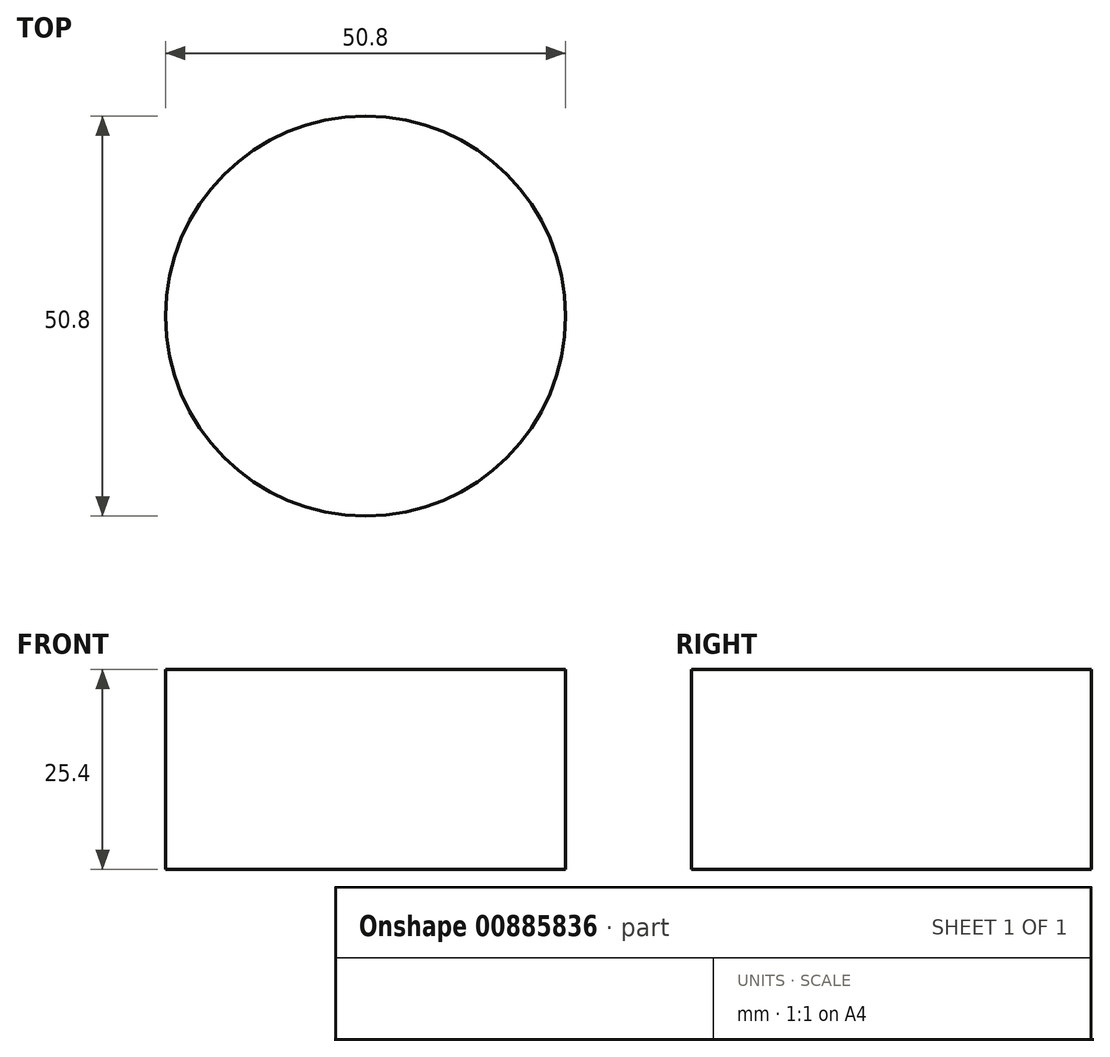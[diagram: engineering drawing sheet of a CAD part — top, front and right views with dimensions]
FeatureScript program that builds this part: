
annotation { "Feature Type Name" : "Feature", "Feature Type Description" : "" }
export const myFeature = defineFeature(function(context is Context, id is Id, definition is map)
    precondition{}
    {
        {
            var Q0;
            Q0=qCreatedBy(makeId("Top.planeOp"),FACE);
            var sketch = newSketch(context, id + "F0", { "sketchPlane" : qUnion([Q0])});
            skCircle(sketch, "E0", {"center": v(0, 0) * mm, "radius": 25.4 * mm});
            skLineSegment(sketch, "E1", {"start": v(76.15, 347.35) * mm, "end": v(71.93, 342.41) * mm});
            skLineSegment(sketch, "E2", {"start": v(71.93, 342.41) * mm, "end": v(67.97, 337.4) * mm});
            skLineSegment(sketch, "E3", {"start": v(67.97, 337.4) * mm, "end": v(64.3, 332.3) * mm});
            skLineSegment(sketch, "E4", {"start": v(64.3, 332.3) * mm, "end": v(60.92, 327.12) * mm});
            skLineSegment(sketch, "E5", {"start": v(60.92, 327.12) * mm, "end": v(57.86, 321.87) * mm});
            skLineSegment(sketch, "E6", {"start": v(57.86, 321.87) * mm, "end": v(55.17, 316.54) * mm});
            skLineSegment(sketch, "E7", {"start": v(55.17, 316.54) * mm, "end": v(52.9, 311.13) * mm});
            skLineSegment(sketch, "E8", {"start": v(52.9, 311.13) * mm, "end": v(51.25, 305.61) * mm});
            skLineSegment(sketch, "E9", {"start": v(51.25, 305.61) * mm, "end": v(49.26, 300.15) * mm});
            skLineSegment(sketch, "E10", {"start": v(49.26, 300.15) * mm, "end": v(35.97, 296.27) * mm});
            skLineSegment(sketch, "E11", {"start": v(35.97, 296.27) * mm, "end": v(24, 303.22) * mm});
            skLineSegment(sketch, "E12", {"start": v(24, 303.22) * mm, "end": v(23.37, 309) * mm});
            skLineSegment(sketch, "E13", {"start": v(23.37, 309) * mm, "end": v(23.09, 314.75) * mm});
            skLineSegment(sketch, "E14", {"start": v(23.09, 314.75) * mm, "end": v(22.19, 320.54) * mm});
            skLineSegment(sketch, "E15", {"start": v(22.19, 320.54) * mm, "end": v(20.84, 326.36) * mm});
            skLineSegment(sketch, "E16", {"start": v(20.84, 326.36) * mm, "end": v(19.13, 332.19) * mm});
            skLineSegment(sketch, "E17", {"start": v(19.13, 332.19) * mm, "end": v(17.1, 338.02) * mm});
            skLineSegment(sketch, "E18", {"start": v(17.1, 338.02) * mm, "end": v(14.74, 343.85) * mm});
            skLineSegment(sketch, "E19", {"start": v(14.74, 343.85) * mm, "end": v(12.1, 349.68) * mm});
            skLineSegment(sketch, "E20", {"start": v(12.1, 349.68) * mm, "end": v(9.2, 355.48) * mm});
            skLineSegment(sketch, "E21", {"start": v(9.2, 355.48) * mm, "end": v(-9.2, 355.48) * mm});
            skLineSegment(sketch, "E22", {"start": v(-9.2, 355.48) * mm, "end": v(-12.1, 349.68) * mm});
            skLineSegment(sketch, "E23", {"start": v(-12.1, 349.68) * mm, "end": v(-14.74, 343.85) * mm});
            skLineSegment(sketch, "E24", {"start": v(-14.74, 343.85) * mm, "end": v(-17.1, 338.02) * mm});
            skLineSegment(sketch, "E25", {"start": v(-17.1, 338.02) * mm, "end": v(-19.13, 332.19) * mm});
            skLineSegment(sketch, "E26", {"start": v(-19.13, 332.19) * mm, "end": v(-20.84, 326.36) * mm});
            skLineSegment(sketch, "E27", {"start": v(-20.84, 326.36) * mm, "end": v(-22.19, 320.54) * mm});
            skLineSegment(sketch, "E28", {"start": v(-22.19, 320.54) * mm, "end": v(-23.09, 314.75) * mm});
            skLineSegment(sketch, "E29", {"start": v(-23.09, 314.75) * mm, "end": v(-23.37, 309) * mm});
            skLineSegment(sketch, "E30", {"start": v(-23.37, 309) * mm, "end": v(-24, 303.22) * mm});
            skLineSegment(sketch, "E31", {"start": v(-24, 303.22) * mm, "end": v(-35.97, 296.27) * mm});
            skLineSegment(sketch, "E32", {"start": v(-35.97, 296.27) * mm, "end": v(-49.26, 300.15) * mm});
            skLineSegment(sketch, "E33", {"start": v(-49.26, 300.15) * mm, "end": v(-51.25, 305.61) * mm});
            skLineSegment(sketch, "E34", {"start": v(-51.25, 305.61) * mm, "end": v(-52.9, 311.13) * mm});
            skLineSegment(sketch, "E35", {"start": v(-52.9, 311.13) * mm, "end": v(-55.17, 316.54) * mm});
            skLineSegment(sketch, "E36", {"start": v(-55.17, 316.54) * mm, "end": v(-57.86, 321.87) * mm});
            skLineSegment(sketch, "E37", {"start": v(-57.86, 321.87) * mm, "end": v(-60.92, 327.12) * mm});
            skLineSegment(sketch, "E38", {"start": v(-60.92, 327.12) * mm, "end": v(-64.3, 332.3) * mm});
            skLineSegment(sketch, "E39", {"start": v(-64.3, 332.3) * mm, "end": v(-67.97, 337.4) * mm});
            skLineSegment(sketch, "E40", {"start": v(-67.97, 337.4) * mm, "end": v(-71.93, 342.41) * mm});
            skLineSegment(sketch, "E41", {"start": v(-71.93, 342.41) * mm, "end": v(-76.15, 347.35) * mm});
            skLineSegment(sketch, "E42", {"start": v(-76.15, 347.35) * mm, "end": v(-94, 342.95) * mm});
            skLineSegment(sketch, "E43", {"start": v(-94, 342.95) * mm, "end": v(-95.44, 336.62) * mm});
            skLineSegment(sketch, "E44", {"start": v(-95.44, 336.62) * mm, "end": v(-96.6, 330.33) * mm});
            skLineSegment(sketch, "E45", {"start": v(-96.6, 330.33) * mm, "end": v(-97.5, 324.11) * mm});
            skLineSegment(sketch, "E46", {"start": v(-97.5, 324.11) * mm, "end": v(-98.08, 317.96) * mm});
            skLineSegment(sketch, "E47", {"start": v(-98.08, 317.96) * mm, "end": v(-98.34, 311.89) * mm});
            skLineSegment(sketch, "E48", {"start": v(-98.34, 311.89) * mm, "end": v(-98.25, 305.92) * mm});
            skLineSegment(sketch, "E49", {"start": v(-98.25, 305.92) * mm, "end": v(-97.74, 300.08) * mm});
            skLineSegment(sketch, "E50", {"start": v(-97.74, 300.08) * mm, "end": v(-96.64, 294.42) * mm});
            skLineSegment(sketch, "E51", {"start": v(-96.64, 294.42) * mm, "end": v(-95.87, 288.66) * mm});
            skLineSegment(sketch, "E52", {"start": v(-95.87, 288.66) * mm, "end": v(-105.83, 279.06) * mm});
            skLineSegment(sketch, "E53", {"start": v(-105.83, 279.06) * mm, "end": v(-119.65, 279.64) * mm});
            skLineSegment(sketch, "E54", {"start": v(-119.65, 279.64) * mm, "end": v(-122.9, 284.47) * mm});
            skLineSegment(sketch, "E55", {"start": v(-122.9, 284.47) * mm, "end": v(-125.83, 289.43) * mm});
            skLineSegment(sketch, "E56", {"start": v(-125.83, 289.43) * mm, "end": v(-129.32, 294.14) * mm});
            skLineSegment(sketch, "E57", {"start": v(-129.32, 294.14) * mm, "end": v(-133.21, 298.66) * mm});
            skLineSegment(sketch, "E58", {"start": v(-133.21, 298.66) * mm, "end": v(-137.43, 303.03) * mm});
            skLineSegment(sketch, "E59", {"start": v(-137.43, 303.03) * mm, "end": v(-141.95, 307.25) * mm});
            skLineSegment(sketch, "E60", {"start": v(-141.95, 307.25) * mm, "end": v(-146.74, 311.32) * mm});
            skLineSegment(sketch, "E61", {"start": v(-146.74, 311.32) * mm, "end": v(-151.78, 315.25) * mm});
            skLineSegment(sketch, "E62", {"start": v(-151.78, 315.25) * mm, "end": v(-157.06, 319.03) * mm});
            skLineSegment(sketch, "E63", {"start": v(-157.06, 319.03) * mm, "end": v(-173.34, 310.5) * mm});
            skLineSegment(sketch, "E64", {"start": v(-173.34, 310.5) * mm, "end": v(-173.22, 304) * mm});
            skLineSegment(sketch, "E65", {"start": v(-173.22, 304) * mm, "end": v(-172.85, 297.62) * mm});
            skLineSegment(sketch, "E66", {"start": v(-172.85, 297.62) * mm, "end": v(-172.22, 291.36) * mm});
            skLineSegment(sketch, "E67", {"start": v(-172.22, 291.36) * mm, "end": v(-171.32, 285.25) * mm});
            skLineSegment(sketch, "E68", {"start": v(-171.32, 285.25) * mm, "end": v(-170.12, 279.3) * mm});
            skLineSegment(sketch, "E69", {"start": v(-170.12, 279.3) * mm, "end": v(-168.6, 273.52) * mm});
            skLineSegment(sketch, "E70", {"start": v(-168.6, 273.52) * mm, "end": v(-166.72, 267.97) * mm});
            skLineSegment(sketch, "E71", {"start": v(-166.72, 267.97) * mm, "end": v(-164.3, 262.74) * mm});
            skLineSegment(sketch, "E72", {"start": v(-164.3, 262.74) * mm, "end": v(-162.17, 257.33) * mm});
            skLineSegment(sketch, "E73", {"start": v(-162.17, 257.33) * mm, "end": v(-169.54, 245.62) * mm});
            skLineSegment(sketch, "E74", {"start": v(-169.54, 245.62) * mm, "end": v(-183.1, 242.88) * mm});
            skLineSegment(sketch, "E75", {"start": v(-183.1, 242.88) * mm, "end": v(-187.4, 246.79) * mm});
            skLineSegment(sketch, "E76", {"start": v(-187.4, 246.79) * mm, "end": v(-191.43, 250.9) * mm});
            skLineSegment(sketch, "E77", {"start": v(-191.43, 250.9) * mm, "end": v(-195.95, 254.64) * mm});
            skLineSegment(sketch, "E78", {"start": v(-195.95, 254.64) * mm, "end": v(-200.81, 258.1) * mm});
            skLineSegment(sketch, "E79", {"start": v(-200.81, 258.1) * mm, "end": v(-205.96, 261.34) * mm});
            skLineSegment(sketch, "E80", {"start": v(-205.96, 261.34) * mm, "end": v(-211.36, 264.35) * mm});
            skLineSegment(sketch, "E81", {"start": v(-211.36, 264.35) * mm, "end": v(-216.98, 267.16) * mm});
            skLineSegment(sketch, "E82", {"start": v(-216.98, 267.16) * mm, "end": v(-222.82, 269.76) * mm});
            skLineSegment(sketch, "E83", {"start": v(-222.82, 269.76) * mm, "end": v(-228.85, 272.18) * mm});
            skLineSegment(sketch, "E84", {"start": v(-228.85, 272.18) * mm, "end": v(-242.6, 259.99) * mm});
            skLineSegment(sketch, "E85", {"start": v(-242.6, 259.99) * mm, "end": v(-240.94, 253.7) * mm});
            skLineSegment(sketch, "E86", {"start": v(-240.94, 253.7) * mm, "end": v(-239.05, 247.6) * mm});
            skLineSegment(sketch, "E87", {"start": v(-239.05, 247.6) * mm, "end": v(-236.94, 241.68) * mm});
            skLineSegment(sketch, "E88", {"start": v(-236.94, 241.68) * mm, "end": v(-234.6, 235.96) * mm});
            skLineSegment(sketch, "E89", {"start": v(-234.6, 235.96) * mm, "end": v(-232.02, 230.46) * mm});
            skLineSegment(sketch, "E90", {"start": v(-232.02, 230.46) * mm, "end": v(-229.17, 225.22) * mm});
            skLineSegment(sketch, "E91", {"start": v(-229.17, 225.22) * mm, "end": v(-226, 220.28) * mm});
            skLineSegment(sketch, "E92", {"start": v(-226, 220.28) * mm, "end": v(-222.4, 215.79) * mm});
            skLineSegment(sketch, "E93", {"start": v(-222.4, 215.79) * mm, "end": v(-219.04, 211.04) * mm});
            skLineSegment(sketch, "E94", {"start": v(-219.04, 211.04) * mm, "end": v(-223.4, 197.9) * mm});
            skLineSegment(sketch, "E95", {"start": v(-223.4, 197.9) * mm, "end": v(-235.9, 192) * mm});
            skLineSegment(sketch, "E96", {"start": v(-235.9, 192) * mm, "end": v(-241.02, 194.77) * mm});
            skLineSegment(sketch, "E97", {"start": v(-241.02, 194.77) * mm, "end": v(-245.92, 197.8) * mm});
            skLineSegment(sketch, "E98", {"start": v(-245.92, 197.8) * mm, "end": v(-251.2, 200.35) * mm});
            skLineSegment(sketch, "E99", {"start": v(-251.2, 200.35) * mm, "end": v(-256.75, 202.55) * mm});
            skLineSegment(sketch, "E100", {"start": v(-256.75, 202.55) * mm, "end": v(-262.52, 204.45) * mm});
            skLineSegment(sketch, "E101", {"start": v(-262.52, 204.45) * mm, "end": v(-268.48, 206.09) * mm});
            skLineSegment(sketch, "E102", {"start": v(-268.48, 206.09) * mm, "end": v(-274.61, 207.47) * mm});
            skLineSegment(sketch, "E103", {"start": v(-274.61, 207.47) * mm, "end": v(-280.9, 208.6) * mm});
            skLineSegment(sketch, "E104", {"start": v(-280.9, 208.6) * mm, "end": v(-287.33, 209.5) * mm});
            skLineSegment(sketch, "E105", {"start": v(-287.33, 209.5) * mm, "end": v(-297.78, 194.37) * mm});
            skLineSegment(sketch, "E106", {"start": v(-297.78, 194.37) * mm, "end": v(-294.65, 188.67) * mm});
            skLineSegment(sketch, "E107", {"start": v(-294.65, 188.67) * mm, "end": v(-291.36, 183.2) * mm});
            skLineSegment(sketch, "E108", {"start": v(-291.36, 183.2) * mm, "end": v(-287.9, 177.95) * mm});
            skLineSegment(sketch, "E109", {"start": v(-287.9, 177.95) * mm, "end": v(-284.26, 172.96) * mm});
            skLineSegment(sketch, "E110", {"start": v(-284.26, 172.96) * mm, "end": v(-280.43, 168.24) * mm});
            skLineSegment(sketch, "E111", {"start": v(-280.43, 168.24) * mm, "end": v(-276.4, 163.83) * mm});
            skLineSegment(sketch, "E112", {"start": v(-276.4, 163.83) * mm, "end": v(-272.15, 159.8) * mm});
            skLineSegment(sketch, "E113", {"start": v(-272.15, 159.8) * mm, "end": v(-267.58, 156.3) * mm});
            skLineSegment(sketch, "E114", {"start": v(-267.58, 156.3) * mm, "end": v(-263.18, 152.49) * mm});
            skLineSegment(sketch, "E115", {"start": v(-263.18, 152.49) * mm, "end": v(-264.26, 138.7) * mm});
            skLineSegment(sketch, "E116", {"start": v(-264.26, 138.7) * mm, "end": v(-275, 129.97) * mm});
            skLineSegment(sketch, "E117", {"start": v(-275, 129.97) * mm, "end": v(-280.63, 131.43) * mm});
            skLineSegment(sketch, "E118", {"start": v(-280.63, 131.43) * mm, "end": v(-286.1, 133.2) * mm});
            skLineSegment(sketch, "E119", {"start": v(-286.1, 133.2) * mm, "end": v(-291.85, 134.41) * mm});
            skLineSegment(sketch, "E120", {"start": v(-291.85, 134.41) * mm, "end": v(-297.76, 135.22) * mm});
            skLineSegment(sketch, "E121", {"start": v(-297.76, 135.22) * mm, "end": v(-303.82, 135.69) * mm});
            skLineSegment(sketch, "E122", {"start": v(-303.82, 135.69) * mm, "end": v(-310, 135.85) * mm});
            skLineSegment(sketch, "E123", {"start": v(-310, 135.85) * mm, "end": v(-316.28, 135.72) * mm});
            skLineSegment(sketch, "E124", {"start": v(-316.28, 135.72) * mm, "end": v(-322.66, 135.32) * mm});
            skLineSegment(sketch, "E125", {"start": v(-322.66, 135.32) * mm, "end": v(-329.12, 134.65) * mm});
            skLineSegment(sketch, "E126", {"start": v(-329.12, 134.65) * mm, "end": v(-335.64, 117.46) * mm});
            skLineSegment(sketch, "E127", {"start": v(-335.64, 117.46) * mm, "end": v(-331.25, 112.68) * mm});
            skLineSegment(sketch, "E128", {"start": v(-331.25, 112.68) * mm, "end": v(-326.74, 108.15) * mm});
            skLineSegment(sketch, "E129", {"start": v(-326.74, 108.15) * mm, "end": v(-322.12, 103.88) * mm});
            skLineSegment(sketch, "E130", {"start": v(-322.12, 103.88) * mm, "end": v(-317.39, 99.9) * mm});
            skLineSegment(sketch, "E131", {"start": v(-317.39, 99.9) * mm, "end": v(-312.54, 96.24) * mm});
            skLineSegment(sketch, "E132", {"start": v(-312.54, 96.24) * mm, "end": v(-307.58, 92.92) * mm});
            skLineSegment(sketch, "E133", {"start": v(-307.58, 92.92) * mm, "end": v(-302.48, 90.02) * mm});
            skLineSegment(sketch, "E134", {"start": v(-302.48, 90.02) * mm, "end": v(-297.2, 87.72) * mm});
            skLineSegment(sketch, "E135", {"start": v(-297.2, 87.72) * mm, "end": v(-292.02, 85.08) * mm});
            skLineSegment(sketch, "E136", {"start": v(-292.02, 85.08) * mm, "end": v(-289.78, 71.42) * mm});
            skLineSegment(sketch, "E137", {"start": v(-289.78, 71.42) * mm, "end": v(-298.11, 60.38) * mm});
            skLineSegment(sketch, "E138", {"start": v(-298.11, 60.38) * mm, "end": v(-303.93, 60.45) * mm});
            skLineSegment(sketch, "E139", {"start": v(-303.93, 60.45) * mm, "end": v(-309.67, 60.86) * mm});
            skLineSegment(sketch, "E140", {"start": v(-309.67, 60.86) * mm, "end": v(-315.53, 60.66) * mm});
            skLineSegment(sketch, "E141", {"start": v(-315.53, 60.66) * mm, "end": v(-321.47, 60.03) * mm});
            skLineSegment(sketch, "E142", {"start": v(-321.47, 60.03) * mm, "end": v(-327.46, 59.04) * mm});
            skLineSegment(sketch, "E143", {"start": v(-327.46, 59.04) * mm, "end": v(-333.5, 57.71) * mm});
            skLineSegment(sketch, "E144", {"start": v(-333.5, 57.71) * mm, "end": v(-339.57, 56.08) * mm});
            skLineSegment(sketch, "E145", {"start": v(-339.57, 56.08) * mm, "end": v(-345.67, 54.17) * mm});
            skLineSegment(sketch, "E146", {"start": v(-345.67, 54.17) * mm, "end": v(-351.78, 51.97) * mm});
            skLineSegment(sketch, "E147", {"start": v(-351.78, 51.97) * mm, "end": v(-354, 33.72) * mm});
            skLineSegment(sketch, "E148", {"start": v(-354, 33.72) * mm, "end": v(-348.59, 30.13) * mm});
            skLineSegment(sketch, "E149", {"start": v(-348.59, 30.13) * mm, "end": v(-343.12, 26.8) * mm});
            skLineSegment(sketch, "E150", {"start": v(-343.12, 26.8) * mm, "end": v(-337.62, 23.78) * mm});
            skLineSegment(sketch, "E151", {"start": v(-337.62, 23.78) * mm, "end": v(-332.07, 21.05) * mm});
            skLineSegment(sketch, "E152", {"start": v(-332.07, 21.05) * mm, "end": v(-326.5, 18.65) * mm});
            skLineSegment(sketch, "E153", {"start": v(-326.5, 18.65) * mm, "end": v(-320.88, 16.61) * mm});
            skLineSegment(sketch, "E154", {"start": v(-320.88, 16.61) * mm, "end": v(-315.24, 15.02) * mm});
            skLineSegment(sketch, "E155", {"start": v(-315.24, 15.02) * mm, "end": v(-309.56, 14.04) * mm});
            skLineSegment(sketch, "E156", {"start": v(-309.56, 14.04) * mm, "end": v(-303.9, 12.72) * mm});
            skLineSegment(sketch, "E157", {"start": v(-303.9, 12.72) * mm, "end": v(-298.45, 0) * mm});
            skLineSegment(sketch, "E158", {"start": v(-298.45, 0) * mm, "end": v(-303.9, -12.72) * mm});
            skLineSegment(sketch, "E159", {"start": v(-303.9, -12.72) * mm, "end": v(-309.56, -14.04) * mm});
            skLineSegment(sketch, "E160", {"start": v(-309.56, -14.04) * mm, "end": v(-315.24, -15.02) * mm});
            skLineSegment(sketch, "E161", {"start": v(-315.24, -15.02) * mm, "end": v(-320.88, -16.61) * mm});
            skLineSegment(sketch, "E162", {"start": v(-320.88, -16.61) * mm, "end": v(-326.5, -18.65) * mm});
            skLineSegment(sketch, "E163", {"start": v(-326.5, -18.65) * mm, "end": v(-332.07, -21.05) * mm});
            skLineSegment(sketch, "E164", {"start": v(-332.07, -21.05) * mm, "end": v(-337.62, -23.78) * mm});
            skLineSegment(sketch, "E165", {"start": v(-337.62, -23.78) * mm, "end": v(-343.12, -26.8) * mm});
            skLineSegment(sketch, "E166", {"start": v(-343.12, -26.8) * mm, "end": v(-348.59, -30.13) * mm});
            skLineSegment(sketch, "E167", {"start": v(-348.59, -30.13) * mm, "end": v(-354, -33.72) * mm});
            skLineSegment(sketch, "E168", {"start": v(-354, -33.72) * mm, "end": v(-351.78, -51.97) * mm});
            skLineSegment(sketch, "E169", {"start": v(-351.78, -51.97) * mm, "end": v(-345.67, -54.17) * mm});
            skLineSegment(sketch, "E170", {"start": v(-345.67, -54.17) * mm, "end": v(-339.57, -56.08) * mm});
            skLineSegment(sketch, "E171", {"start": v(-339.57, -56.08) * mm, "end": v(-333.5, -57.71) * mm});
            skLineSegment(sketch, "E172", {"start": v(-333.5, -57.71) * mm, "end": v(-327.46, -59.04) * mm});
            skLineSegment(sketch, "E173", {"start": v(-327.46, -59.04) * mm, "end": v(-321.47, -60.03) * mm});
            skLineSegment(sketch, "E174", {"start": v(-321.47, -60.03) * mm, "end": v(-315.53, -60.66) * mm});
            skLineSegment(sketch, "E175", {"start": v(-315.53, -60.66) * mm, "end": v(-309.67, -60.86) * mm});
            skLineSegment(sketch, "E176", {"start": v(-309.67, -60.86) * mm, "end": v(-303.93, -60.45) * mm});
            skLineSegment(sketch, "E177", {"start": v(-303.93, -60.45) * mm, "end": v(-298.11, -60.38) * mm});
            skLineSegment(sketch, "E178", {"start": v(-298.11, -60.38) * mm, "end": v(-289.78, -71.42) * mm});
            skLineSegment(sketch, "E179", {"start": v(-289.78, -71.42) * mm, "end": v(-292.02, -85.08) * mm});
            skLineSegment(sketch, "E180", {"start": v(-292.02, -85.08) * mm, "end": v(-297.2, -87.72) * mm});
            skLineSegment(sketch, "E181", {"start": v(-297.2, -87.72) * mm, "end": v(-302.48, -90.02) * mm});
            skLineSegment(sketch, "E182", {"start": v(-302.48, -90.02) * mm, "end": v(-307.58, -92.92) * mm});
            skLineSegment(sketch, "E183", {"start": v(-307.58, -92.92) * mm, "end": v(-312.54, -96.24) * mm});
            skLineSegment(sketch, "E184", {"start": v(-312.54, -96.24) * mm, "end": v(-317.39, -99.9) * mm});
            skLineSegment(sketch, "E185", {"start": v(-317.39, -99.9) * mm, "end": v(-322.12, -103.88) * mm});
            skLineSegment(sketch, "E186", {"start": v(-322.12, -103.88) * mm, "end": v(-326.74, -108.15) * mm});
            skLineSegment(sketch, "E187", {"start": v(-326.74, -108.15) * mm, "end": v(-331.25, -112.68) * mm});
            skLineSegment(sketch, "E188", {"start": v(-331.25, -112.68) * mm, "end": v(-335.64, -117.46) * mm});
            skLineSegment(sketch, "E189", {"start": v(-335.64, -117.46) * mm, "end": v(-329.12, -134.65) * mm});
            skLineSegment(sketch, "E190", {"start": v(-329.12, -134.65) * mm, "end": v(-322.66, -135.32) * mm});
            skLineSegment(sketch, "E191", {"start": v(-322.66, -135.32) * mm, "end": v(-316.28, -135.72) * mm});
            skLineSegment(sketch, "E192", {"start": v(-316.28, -135.72) * mm, "end": v(-310, -135.85) * mm});
            skLineSegment(sketch, "E193", {"start": v(-310, -135.85) * mm, "end": v(-303.82, -135.69) * mm});
            skLineSegment(sketch, "E194", {"start": v(-303.82, -135.69) * mm, "end": v(-297.76, -135.22) * mm});
            skLineSegment(sketch, "E195", {"start": v(-297.76, -135.22) * mm, "end": v(-291.85, -134.41) * mm});
            skLineSegment(sketch, "E196", {"start": v(-291.85, -134.41) * mm, "end": v(-286.1, -133.2) * mm});
            skLineSegment(sketch, "E197", {"start": v(-286.1, -133.2) * mm, "end": v(-280.63, -131.43) * mm});
            skLineSegment(sketch, "E198", {"start": v(-280.63, -131.43) * mm, "end": v(-275, -129.97) * mm});
            skLineSegment(sketch, "E199", {"start": v(-275, -129.97) * mm, "end": v(-264.26, -138.7) * mm});
            skLineSegment(sketch, "E200", {"start": v(-264.26, -138.7) * mm, "end": v(-263.18, -152.49) * mm});
            skLineSegment(sketch, "E201", {"start": v(-263.18, -152.49) * mm, "end": v(-267.58, -156.3) * mm});
            skLineSegment(sketch, "E202", {"start": v(-267.58, -156.3) * mm, "end": v(-272.15, -159.8) * mm});
            skLineSegment(sketch, "E203", {"start": v(-272.15, -159.8) * mm, "end": v(-276.4, -163.83) * mm});
            skLineSegment(sketch, "E204", {"start": v(-276.4, -163.83) * mm, "end": v(-280.43, -168.24) * mm});
            skLineSegment(sketch, "E205", {"start": v(-280.43, -168.24) * mm, "end": v(-284.26, -172.96) * mm});
            skLineSegment(sketch, "E206", {"start": v(-284.26, -172.96) * mm, "end": v(-287.9, -177.95) * mm});
            skLineSegment(sketch, "E207", {"start": v(-287.9, -177.95) * mm, "end": v(-291.36, -183.2) * mm});
            skLineSegment(sketch, "E208", {"start": v(-291.36, -183.2) * mm, "end": v(-294.65, -188.67) * mm});
            skLineSegment(sketch, "E209", {"start": v(-294.65, -188.67) * mm, "end": v(-297.78, -194.37) * mm});
            skLineSegment(sketch, "E210", {"start": v(-297.78, -194.37) * mm, "end": v(-287.33, -209.5) * mm});
            skLineSegment(sketch, "E211", {"start": v(-287.33, -209.5) * mm, "end": v(-280.9, -208.6) * mm});
            skLineSegment(sketch, "E212", {"start": v(-280.9, -208.6) * mm, "end": v(-274.61, -207.47) * mm});
            skLineSegment(sketch, "E213", {"start": v(-274.61, -207.47) * mm, "end": v(-268.48, -206.09) * mm});
            skLineSegment(sketch, "E214", {"start": v(-268.48, -206.09) * mm, "end": v(-262.52, -204.45) * mm});
            skLineSegment(sketch, "E215", {"start": v(-262.52, -204.45) * mm, "end": v(-256.75, -202.55) * mm});
            skLineSegment(sketch, "E216", {"start": v(-256.75, -202.55) * mm, "end": v(-251.2, -200.35) * mm});
            skLineSegment(sketch, "E217", {"start": v(-251.2, -200.35) * mm, "end": v(-245.92, -197.8) * mm});
            skLineSegment(sketch, "E218", {"start": v(-245.92, -197.8) * mm, "end": v(-241.02, -194.77) * mm});
            skLineSegment(sketch, "E219", {"start": v(-241.02, -194.77) * mm, "end": v(-235.9, -192) * mm});
            skLineSegment(sketch, "E220", {"start": v(-235.9, -192) * mm, "end": v(-223.4, -197.9) * mm});
            skLineSegment(sketch, "E221", {"start": v(-223.4, -197.9) * mm, "end": v(-219.04, -211.04) * mm});
            skLineSegment(sketch, "E222", {"start": v(-219.04, -211.04) * mm, "end": v(-222.4, -215.79) * mm});
            skLineSegment(sketch, "E223", {"start": v(-222.4, -215.79) * mm, "end": v(-226, -220.28) * mm});
            skLineSegment(sketch, "E224", {"start": v(-226, -220.28) * mm, "end": v(-229.17, -225.22) * mm});
            skLineSegment(sketch, "E225", {"start": v(-229.17, -225.22) * mm, "end": v(-232.02, -230.46) * mm});
            skLineSegment(sketch, "E226", {"start": v(-232.02, -230.46) * mm, "end": v(-234.6, -235.96) * mm});
            skLineSegment(sketch, "E227", {"start": v(-234.6, -235.96) * mm, "end": v(-236.94, -241.68) * mm});
            skLineSegment(sketch, "E228", {"start": v(-236.94, -241.68) * mm, "end": v(-239.05, -247.6) * mm});
            skLineSegment(sketch, "E229", {"start": v(-239.05, -247.6) * mm, "end": v(-240.94, -253.7) * mm});
            skLineSegment(sketch, "E230", {"start": v(-240.94, -253.7) * mm, "end": v(-242.6, -259.99) * mm});
            skLineSegment(sketch, "E231", {"start": v(-242.6, -259.99) * mm, "end": v(-228.85, -272.18) * mm});
            skLineSegment(sketch, "E232", {"start": v(-228.85, -272.18) * mm, "end": v(-222.82, -269.76) * mm});
            skLineSegment(sketch, "E233", {"start": v(-222.82, -269.76) * mm, "end": v(-216.98, -267.16) * mm});
            skLineSegment(sketch, "E234", {"start": v(-216.98, -267.16) * mm, "end": v(-211.36, -264.35) * mm});
            skLineSegment(sketch, "E235", {"start": v(-211.36, -264.35) * mm, "end": v(-205.96, -261.34) * mm});
            skLineSegment(sketch, "E236", {"start": v(-205.96, -261.34) * mm, "end": v(-200.81, -258.1) * mm});
            skLineSegment(sketch, "E237", {"start": v(-200.81, -258.1) * mm, "end": v(-195.95, -254.64) * mm});
            skLineSegment(sketch, "E238", {"start": v(-195.95, -254.64) * mm, "end": v(-191.43, -250.9) * mm});
            skLineSegment(sketch, "E239", {"start": v(-191.43, -250.9) * mm, "end": v(-187.4, -246.79) * mm});
            skLineSegment(sketch, "E240", {"start": v(-187.4, -246.79) * mm, "end": v(-183.1, -242.88) * mm});
            skLineSegment(sketch, "E241", {"start": v(-183.1, -242.88) * mm, "end": v(-169.54, -245.62) * mm});
            skLineSegment(sketch, "E242", {"start": v(-169.54, -245.62) * mm, "end": v(-162.17, -257.33) * mm});
            skLineSegment(sketch, "E243", {"start": v(-162.17, -257.33) * mm, "end": v(-164.3, -262.74) * mm});
            skLineSegment(sketch, "E244", {"start": v(-164.3, -262.74) * mm, "end": v(-166.72, -267.97) * mm});
            skLineSegment(sketch, "E245", {"start": v(-166.72, -267.97) * mm, "end": v(-168.6, -273.52) * mm});
            skLineSegment(sketch, "E246", {"start": v(-168.6, -273.52) * mm, "end": v(-170.12, -279.3) * mm});
            skLineSegment(sketch, "E247", {"start": v(-170.12, -279.3) * mm, "end": v(-171.32, -285.25) * mm});
            skLineSegment(sketch, "E248", {"start": v(-171.32, -285.25) * mm, "end": v(-172.22, -291.36) * mm});
            skLineSegment(sketch, "E249", {"start": v(-172.22, -291.36) * mm, "end": v(-172.85, -297.62) * mm});
            skLineSegment(sketch, "E250", {"start": v(-172.85, -297.62) * mm, "end": v(-173.22, -304) * mm});
            skLineSegment(sketch, "E251", {"start": v(-173.22, -304) * mm, "end": v(-173.34, -310.5) * mm});
            skLineSegment(sketch, "E252", {"start": v(-173.34, -310.5) * mm, "end": v(-157.06, -319.03) * mm});
            skLineSegment(sketch, "E253", {"start": v(-157.06, -319.03) * mm, "end": v(-151.78, -315.25) * mm});
            skLineSegment(sketch, "E254", {"start": v(-151.78, -315.25) * mm, "end": v(-146.74, -311.32) * mm});
            skLineSegment(sketch, "E255", {"start": v(-146.74, -311.32) * mm, "end": v(-141.95, -307.25) * mm});
            skLineSegment(sketch, "E256", {"start": v(-141.95, -307.25) * mm, "end": v(-137.43, -303.03) * mm});
            skLineSegment(sketch, "E257", {"start": v(-137.43, -303.03) * mm, "end": v(-133.21, -298.66) * mm});
            skLineSegment(sketch, "E258", {"start": v(-133.21, -298.66) * mm, "end": v(-129.32, -294.14) * mm});
            skLineSegment(sketch, "E259", {"start": v(-129.32, -294.14) * mm, "end": v(-125.83, -289.43) * mm});
            skLineSegment(sketch, "E260", {"start": v(-125.83, -289.43) * mm, "end": v(-122.9, -284.47) * mm});
            skLineSegment(sketch, "E261", {"start": v(-122.9, -284.47) * mm, "end": v(-119.65, -279.64) * mm});
            skLineSegment(sketch, "E262", {"start": v(-119.65, -279.64) * mm, "end": v(-105.83, -279.06) * mm});
            skLineSegment(sketch, "E263", {"start": v(-105.83, -279.06) * mm, "end": v(-95.87, -288.66) * mm});
            skLineSegment(sketch, "E264", {"start": v(-95.87, -288.66) * mm, "end": v(-96.64, -294.42) * mm});
            skLineSegment(sketch, "E265", {"start": v(-96.64, -294.42) * mm, "end": v(-97.74, -300.08) * mm});
            skLineSegment(sketch, "E266", {"start": v(-97.74, -300.08) * mm, "end": v(-98.25, -305.92) * mm});
            skLineSegment(sketch, "E267", {"start": v(-98.25, -305.92) * mm, "end": v(-98.34, -311.89) * mm});
            skLineSegment(sketch, "E268", {"start": v(-98.34, -311.89) * mm, "end": v(-98.08, -317.96) * mm});
            skLineSegment(sketch, "E269", {"start": v(-98.08, -317.96) * mm, "end": v(-97.5, -324.11) * mm});
            skLineSegment(sketch, "E270", {"start": v(-97.5, -324.11) * mm, "end": v(-96.6, -330.33) * mm});
            skLineSegment(sketch, "E271", {"start": v(-96.6, -330.33) * mm, "end": v(-95.44, -336.62) * mm});
            skLineSegment(sketch, "E272", {"start": v(-95.44, -336.62) * mm, "end": v(-94, -342.95) * mm});
            skLineSegment(sketch, "E273", {"start": v(-94, -342.95) * mm, "end": v(-76.15, -347.35) * mm});
            skLineSegment(sketch, "E274", {"start": v(-76.15, -347.35) * mm, "end": v(-71.93, -342.41) * mm});
            skLineSegment(sketch, "E275", {"start": v(-71.93, -342.41) * mm, "end": v(-67.97, -337.4) * mm});
            skLineSegment(sketch, "E276", {"start": v(-67.97, -337.4) * mm, "end": v(-64.3, -332.3) * mm});
            skLineSegment(sketch, "E277", {"start": v(-64.3, -332.3) * mm, "end": v(-60.92, -327.12) * mm});
            skLineSegment(sketch, "E278", {"start": v(-60.92, -327.12) * mm, "end": v(-57.86, -321.87) * mm});
            skLineSegment(sketch, "E279", {"start": v(-57.86, -321.87) * mm, "end": v(-55.17, -316.54) * mm});
            skLineSegment(sketch, "E280", {"start": v(-55.17, -316.54) * mm, "end": v(-52.9, -311.13) * mm});
            skLineSegment(sketch, "E281", {"start": v(-52.9, -311.13) * mm, "end": v(-51.25, -305.61) * mm});
            skLineSegment(sketch, "E282", {"start": v(-51.25, -305.61) * mm, "end": v(-49.26, -300.15) * mm});
            skLineSegment(sketch, "E283", {"start": v(-49.26, -300.15) * mm, "end": v(-35.97, -296.27) * mm});
            skLineSegment(sketch, "E284", {"start": v(-35.97, -296.27) * mm, "end": v(-24, -303.22) * mm});
            skLineSegment(sketch, "E285", {"start": v(-24, -303.22) * mm, "end": v(-23.37, -309) * mm});
            skLineSegment(sketch, "E286", {"start": v(-23.37, -309) * mm, "end": v(-23.09, -314.75) * mm});
            skLineSegment(sketch, "E287", {"start": v(-23.09, -314.75) * mm, "end": v(-22.19, -320.54) * mm});
            skLineSegment(sketch, "E288", {"start": v(-22.19, -320.54) * mm, "end": v(-20.84, -326.36) * mm});
            skLineSegment(sketch, "E289", {"start": v(-20.84, -326.36) * mm, "end": v(-19.13, -332.19) * mm});
            skLineSegment(sketch, "E290", {"start": v(-19.13, -332.19) * mm, "end": v(-17.1, -338.02) * mm});
            skLineSegment(sketch, "E291", {"start": v(-17.1, -338.02) * mm, "end": v(-14.74, -343.85) * mm});
            skLineSegment(sketch, "E292", {"start": v(-14.74, -343.85) * mm, "end": v(-12.1, -349.68) * mm});
            skLineSegment(sketch, "E293", {"start": v(-12.1, -349.68) * mm, "end": v(-9.2, -355.48) * mm});
            skLineSegment(sketch, "E294", {"start": v(-9.2, -355.48) * mm, "end": v(9.2, -355.48) * mm});
            skLineSegment(sketch, "E295", {"start": v(9.2, -355.48) * mm, "end": v(12.1, -349.68) * mm});
            skLineSegment(sketch, "E296", {"start": v(12.1, -349.68) * mm, "end": v(14.74, -343.85) * mm});
            skLineSegment(sketch, "E297", {"start": v(14.74, -343.85) * mm, "end": v(17.1, -338.02) * mm});
            skLineSegment(sketch, "E298", {"start": v(17.1, -338.02) * mm, "end": v(19.13, -332.19) * mm});
            skLineSegment(sketch, "E299", {"start": v(19.13, -332.19) * mm, "end": v(20.84, -326.36) * mm});
            skLineSegment(sketch, "E300", {"start": v(20.84, -326.36) * mm, "end": v(22.19, -320.54) * mm});
            skLineSegment(sketch, "E301", {"start": v(22.19, -320.54) * mm, "end": v(23.09, -314.75) * mm});
            skLineSegment(sketch, "E302", {"start": v(23.09, -314.75) * mm, "end": v(23.37, -309) * mm});
            skLineSegment(sketch, "E303", {"start": v(23.37, -309) * mm, "end": v(24, -303.22) * mm});
            skLineSegment(sketch, "E304", {"start": v(24, -303.22) * mm, "end": v(35.97, -296.27) * mm});
            skLineSegment(sketch, "E305", {"start": v(35.97, -296.27) * mm, "end": v(49.26, -300.15) * mm});
            skLineSegment(sketch, "E306", {"start": v(49.26, -300.15) * mm, "end": v(51.25, -305.61) * mm});
            skLineSegment(sketch, "E307", {"start": v(51.25, -305.61) * mm, "end": v(52.9, -311.13) * mm});
            skLineSegment(sketch, "E308", {"start": v(52.9, -311.13) * mm, "end": v(55.17, -316.54) * mm});
            skLineSegment(sketch, "E309", {"start": v(55.17, -316.54) * mm, "end": v(57.86, -321.87) * mm});
            skLineSegment(sketch, "E310", {"start": v(57.86, -321.87) * mm, "end": v(60.92, -327.12) * mm});
            skLineSegment(sketch, "E311", {"start": v(60.92, -327.12) * mm, "end": v(64.3, -332.3) * mm});
            skLineSegment(sketch, "E312", {"start": v(64.3, -332.3) * mm, "end": v(67.97, -337.4) * mm});
            skLineSegment(sketch, "E313", {"start": v(67.97, -337.4) * mm, "end": v(71.93, -342.41) * mm});
            skLineSegment(sketch, "E314", {"start": v(71.93, -342.41) * mm, "end": v(76.15, -347.35) * mm});
            skLineSegment(sketch, "E315", {"start": v(76.15, -347.35) * mm, "end": v(94, -342.95) * mm});
            skLineSegment(sketch, "E316", {"start": v(94, -342.95) * mm, "end": v(95.44, -336.62) * mm});
            skLineSegment(sketch, "E317", {"start": v(95.44, -336.62) * mm, "end": v(96.6, -330.33) * mm});
            skLineSegment(sketch, "E318", {"start": v(96.6, -330.33) * mm, "end": v(97.5, -324.11) * mm});
            skLineSegment(sketch, "E319", {"start": v(97.5, -324.11) * mm, "end": v(98.08, -317.96) * mm});
            skLineSegment(sketch, "E320", {"start": v(98.08, -317.96) * mm, "end": v(98.34, -311.89) * mm});
            skLineSegment(sketch, "E321", {"start": v(98.34, -311.89) * mm, "end": v(98.25, -305.92) * mm});
            skLineSegment(sketch, "E322", {"start": v(98.25, -305.92) * mm, "end": v(97.74, -300.08) * mm});
            skLineSegment(sketch, "E323", {"start": v(97.74, -300.08) * mm, "end": v(96.64, -294.42) * mm});
            skLineSegment(sketch, "E324", {"start": v(96.64, -294.42) * mm, "end": v(95.87, -288.66) * mm});
            skLineSegment(sketch, "E325", {"start": v(95.87, -288.66) * mm, "end": v(105.83, -279.06) * mm});
            skLineSegment(sketch, "E326", {"start": v(105.83, -279.06) * mm, "end": v(119.65, -279.64) * mm});
            skLineSegment(sketch, "E327", {"start": v(119.65, -279.64) * mm, "end": v(122.9, -284.47) * mm});
            skLineSegment(sketch, "E328", {"start": v(122.9, -284.47) * mm, "end": v(125.83, -289.43) * mm});
            skLineSegment(sketch, "E329", {"start": v(125.83, -289.43) * mm, "end": v(129.32, -294.14) * mm});
            skLineSegment(sketch, "E330", {"start": v(129.32, -294.14) * mm, "end": v(133.21, -298.66) * mm});
            skLineSegment(sketch, "E331", {"start": v(133.21, -298.66) * mm, "end": v(137.43, -303.03) * mm});
            skLineSegment(sketch, "E332", {"start": v(137.43, -303.03) * mm, "end": v(141.95, -307.25) * mm});
            skLineSegment(sketch, "E333", {"start": v(141.95, -307.25) * mm, "end": v(146.74, -311.32) * mm});
            skLineSegment(sketch, "E334", {"start": v(146.74, -311.32) * mm, "end": v(151.78, -315.25) * mm});
            skLineSegment(sketch, "E335", {"start": v(151.78, -315.25) * mm, "end": v(157.06, -319.03) * mm});
            skLineSegment(sketch, "E336", {"start": v(157.06, -319.03) * mm, "end": v(173.34, -310.5) * mm});
            skLineSegment(sketch, "E337", {"start": v(173.34, -310.5) * mm, "end": v(173.22, -304) * mm});
            skLineSegment(sketch, "E338", {"start": v(173.22, -304) * mm, "end": v(172.85, -297.62) * mm});
            skLineSegment(sketch, "E339", {"start": v(172.85, -297.62) * mm, "end": v(172.22, -291.36) * mm});
            skLineSegment(sketch, "E340", {"start": v(172.22, -291.36) * mm, "end": v(171.32, -285.25) * mm});
            skLineSegment(sketch, "E341", {"start": v(171.32, -285.25) * mm, "end": v(170.12, -279.3) * mm});
            skLineSegment(sketch, "E342", {"start": v(170.12, -279.3) * mm, "end": v(168.6, -273.52) * mm});
            skLineSegment(sketch, "E343", {"start": v(168.6, -273.52) * mm, "end": v(166.72, -267.97) * mm});
            skLineSegment(sketch, "E344", {"start": v(166.72, -267.97) * mm, "end": v(164.3, -262.74) * mm});
            skLineSegment(sketch, "E345", {"start": v(164.3, -262.74) * mm, "end": v(162.17, -257.33) * mm});
            skLineSegment(sketch, "E346", {"start": v(162.17, -257.33) * mm, "end": v(169.54, -245.62) * mm});
            skLineSegment(sketch, "E347", {"start": v(169.54, -245.62) * mm, "end": v(183.1, -242.88) * mm});
            skLineSegment(sketch, "E348", {"start": v(183.1, -242.88) * mm, "end": v(187.4, -246.79) * mm});
            skLineSegment(sketch, "E349", {"start": v(187.4, -246.79) * mm, "end": v(191.43, -250.9) * mm});
            skLineSegment(sketch, "E350", {"start": v(191.43, -250.9) * mm, "end": v(195.95, -254.64) * mm});
            skLineSegment(sketch, "E351", {"start": v(195.95, -254.64) * mm, "end": v(200.81, -258.1) * mm});
            skLineSegment(sketch, "E352", {"start": v(200.81, -258.1) * mm, "end": v(205.96, -261.34) * mm});
            skLineSegment(sketch, "E353", {"start": v(205.96, -261.34) * mm, "end": v(211.36, -264.35) * mm});
            skLineSegment(sketch, "E354", {"start": v(211.36, -264.35) * mm, "end": v(216.98, -267.16) * mm});
            skLineSegment(sketch, "E355", {"start": v(216.98, -267.16) * mm, "end": v(222.82, -269.76) * mm});
            skLineSegment(sketch, "E356", {"start": v(222.82, -269.76) * mm, "end": v(228.85, -272.18) * mm});
            skLineSegment(sketch, "E357", {"start": v(228.85, -272.18) * mm, "end": v(242.6, -259.99) * mm});
            skLineSegment(sketch, "E358", {"start": v(242.6, -259.99) * mm, "end": v(240.94, -253.7) * mm});
            skLineSegment(sketch, "E359", {"start": v(240.94, -253.7) * mm, "end": v(239.05, -247.6) * mm});
            skLineSegment(sketch, "E360", {"start": v(239.05, -247.6) * mm, "end": v(236.94, -241.68) * mm});
            skLineSegment(sketch, "E361", {"start": v(236.94, -241.68) * mm, "end": v(234.6, -235.96) * mm});
            skLineSegment(sketch, "E362", {"start": v(234.6, -235.96) * mm, "end": v(232.02, -230.46) * mm});
            skLineSegment(sketch, "E363", {"start": v(232.02, -230.46) * mm, "end": v(229.17, -225.22) * mm});
            skLineSegment(sketch, "E364", {"start": v(229.17, -225.22) * mm, "end": v(226, -220.28) * mm});
            skLineSegment(sketch, "E365", {"start": v(226, -220.28) * mm, "end": v(222.4, -215.79) * mm});
            skLineSegment(sketch, "E366", {"start": v(222.4, -215.79) * mm, "end": v(219.04, -211.04) * mm});
            skLineSegment(sketch, "E367", {"start": v(219.04, -211.04) * mm, "end": v(223.4, -197.9) * mm});
            skLineSegment(sketch, "E368", {"start": v(223.4, -197.9) * mm, "end": v(235.9, -192) * mm});
            skLineSegment(sketch, "E369", {"start": v(235.9, -192) * mm, "end": v(241.02, -194.77) * mm});
            skLineSegment(sketch, "E370", {"start": v(241.02, -194.77) * mm, "end": v(245.92, -197.8) * mm});
            skLineSegment(sketch, "E371", {"start": v(245.92, -197.8) * mm, "end": v(251.2, -200.35) * mm});
            skLineSegment(sketch, "E372", {"start": v(251.2, -200.35) * mm, "end": v(256.75, -202.55) * mm});
            skLineSegment(sketch, "E373", {"start": v(256.75, -202.55) * mm, "end": v(262.52, -204.45) * mm});
            skLineSegment(sketch, "E374", {"start": v(262.52, -204.45) * mm, "end": v(268.48, -206.09) * mm});
            skLineSegment(sketch, "E375", {"start": v(268.48, -206.09) * mm, "end": v(274.61, -207.47) * mm});
            skLineSegment(sketch, "E376", {"start": v(274.61, -207.47) * mm, "end": v(280.9, -208.6) * mm});
            skLineSegment(sketch, "E377", {"start": v(280.9, -208.6) * mm, "end": v(287.33, -209.5) * mm});
            skLineSegment(sketch, "E378", {"start": v(287.33, -209.5) * mm, "end": v(297.78, -194.37) * mm});
            skLineSegment(sketch, "E379", {"start": v(297.78, -194.37) * mm, "end": v(294.65, -188.67) * mm});
            skLineSegment(sketch, "E380", {"start": v(294.65, -188.67) * mm, "end": v(291.36, -183.2) * mm});
            skLineSegment(sketch, "E381", {"start": v(291.36, -183.2) * mm, "end": v(287.9, -177.95) * mm});
            skLineSegment(sketch, "E382", {"start": v(287.9, -177.95) * mm, "end": v(284.26, -172.96) * mm});
            skLineSegment(sketch, "E383", {"start": v(284.26, -172.96) * mm, "end": v(280.43, -168.24) * mm});
            skLineSegment(sketch, "E384", {"start": v(280.43, -168.24) * mm, "end": v(276.4, -163.83) * mm});
            skLineSegment(sketch, "E385", {"start": v(276.4, -163.83) * mm, "end": v(272.15, -159.8) * mm});
            skLineSegment(sketch, "E386", {"start": v(272.15, -159.8) * mm, "end": v(267.58, -156.3) * mm});
            skLineSegment(sketch, "E387", {"start": v(267.58, -156.3) * mm, "end": v(263.18, -152.49) * mm});
            skLineSegment(sketch, "E388", {"start": v(263.18, -152.49) * mm, "end": v(264.26, -138.7) * mm});
            skLineSegment(sketch, "E389", {"start": v(264.26, -138.7) * mm, "end": v(275, -129.97) * mm});
            skLineSegment(sketch, "E390", {"start": v(275, -129.97) * mm, "end": v(280.63, -131.43) * mm});
            skLineSegment(sketch, "E391", {"start": v(280.63, -131.43) * mm, "end": v(286.1, -133.2) * mm});
            skLineSegment(sketch, "E392", {"start": v(286.1, -133.2) * mm, "end": v(291.85, -134.41) * mm});
            skLineSegment(sketch, "E393", {"start": v(291.85, -134.41) * mm, "end": v(297.76, -135.22) * mm});
            skLineSegment(sketch, "E394", {"start": v(297.76, -135.22) * mm, "end": v(303.82, -135.69) * mm});
            skLineSegment(sketch, "E395", {"start": v(303.82, -135.69) * mm, "end": v(310, -135.85) * mm});
            skLineSegment(sketch, "E396", {"start": v(310, -135.85) * mm, "end": v(316.28, -135.72) * mm});
            skLineSegment(sketch, "E397", {"start": v(316.28, -135.72) * mm, "end": v(322.66, -135.32) * mm});
            skLineSegment(sketch, "E398", {"start": v(322.66, -135.32) * mm, "end": v(329.12, -134.65) * mm});
            skLineSegment(sketch, "E399", {"start": v(329.12, -134.65) * mm, "end": v(335.64, -117.46) * mm});
            skLineSegment(sketch, "E400", {"start": v(335.64, -117.46) * mm, "end": v(331.25, -112.68) * mm});
            skLineSegment(sketch, "E401", {"start": v(331.25, -112.68) * mm, "end": v(326.74, -108.15) * mm});
            skLineSegment(sketch, "E402", {"start": v(326.74, -108.15) * mm, "end": v(322.12, -103.88) * mm});
            skLineSegment(sketch, "E403", {"start": v(322.12, -103.88) * mm, "end": v(317.39, -99.9) * mm});
            skLineSegment(sketch, "E404", {"start": v(317.39, -99.9) * mm, "end": v(312.54, -96.24) * mm});
            skLineSegment(sketch, "E405", {"start": v(312.54, -96.24) * mm, "end": v(307.58, -92.92) * mm});
            skLineSegment(sketch, "E406", {"start": v(307.58, -92.92) * mm, "end": v(302.48, -90.02) * mm});
            skLineSegment(sketch, "E407", {"start": v(302.48, -90.02) * mm, "end": v(297.2, -87.72) * mm});
            skLineSegment(sketch, "E408", {"start": v(297.2, -87.72) * mm, "end": v(292.02, -85.08) * mm});
            skLineSegment(sketch, "E409", {"start": v(292.02, -85.08) * mm, "end": v(289.78, -71.42) * mm});
            skLineSegment(sketch, "E410", {"start": v(289.78, -71.42) * mm, "end": v(298.11, -60.38) * mm});
            skLineSegment(sketch, "E411", {"start": v(298.11, -60.38) * mm, "end": v(303.93, -60.45) * mm});
            skLineSegment(sketch, "E412", {"start": v(303.93, -60.45) * mm, "end": v(309.67, -60.86) * mm});
            skLineSegment(sketch, "E413", {"start": v(309.67, -60.86) * mm, "end": v(315.53, -60.66) * mm});
            skLineSegment(sketch, "E414", {"start": v(315.53, -60.66) * mm, "end": v(321.47, -60.03) * mm});
            skLineSegment(sketch, "E415", {"start": v(321.47, -60.03) * mm, "end": v(327.46, -59.04) * mm});
            skLineSegment(sketch, "E416", {"start": v(327.46, -59.04) * mm, "end": v(333.5, -57.71) * mm});
            skLineSegment(sketch, "E417", {"start": v(333.5, -57.71) * mm, "end": v(339.57, -56.08) * mm});
            skLineSegment(sketch, "E418", {"start": v(339.57, -56.08) * mm, "end": v(345.67, -54.17) * mm});
            skLineSegment(sketch, "E419", {"start": v(345.67, -54.17) * mm, "end": v(351.78, -51.97) * mm});
            skLineSegment(sketch, "E420", {"start": v(351.78, -51.97) * mm, "end": v(354, -33.72) * mm});
            skLineSegment(sketch, "E421", {"start": v(354, -33.72) * mm, "end": v(348.59, -30.13) * mm});
            skLineSegment(sketch, "E422", {"start": v(348.59, -30.13) * mm, "end": v(343.12, -26.8) * mm});
            skLineSegment(sketch, "E423", {"start": v(343.12, -26.8) * mm, "end": v(337.62, -23.78) * mm});
            skLineSegment(sketch, "E424", {"start": v(337.62, -23.78) * mm, "end": v(332.07, -21.05) * mm});
            skLineSegment(sketch, "E425", {"start": v(332.07, -21.05) * mm, "end": v(326.5, -18.65) * mm});
            skLineSegment(sketch, "E426", {"start": v(326.5, -18.65) * mm, "end": v(320.88, -16.61) * mm});
            skLineSegment(sketch, "E427", {"start": v(320.88, -16.61) * mm, "end": v(315.24, -15.02) * mm});
            skLineSegment(sketch, "E428", {"start": v(315.24, -15.02) * mm, "end": v(309.56, -14.04) * mm});
            skLineSegment(sketch, "E429", {"start": v(309.56, -14.04) * mm, "end": v(303.9, -12.72) * mm});
            skLineSegment(sketch, "E430", {"start": v(303.9, -12.72) * mm, "end": v(298.45, 0) * mm});
            skLineSegment(sketch, "E431", {"start": v(298.45, 0) * mm, "end": v(303.9, 12.72) * mm});
            skLineSegment(sketch, "E432", {"start": v(303.9, 12.72) * mm, "end": v(309.56, 14.04) * mm});
            skLineSegment(sketch, "E433", {"start": v(309.56, 14.04) * mm, "end": v(315.24, 15.02) * mm});
            skLineSegment(sketch, "E434", {"start": v(315.24, 15.02) * mm, "end": v(320.88, 16.61) * mm});
            skLineSegment(sketch, "E435", {"start": v(320.88, 16.61) * mm, "end": v(326.5, 18.65) * mm});
            skLineSegment(sketch, "E436", {"start": v(326.5, 18.65) * mm, "end": v(332.07, 21.05) * mm});
            skLineSegment(sketch, "E437", {"start": v(332.07, 21.05) * mm, "end": v(337.62, 23.78) * mm});
            skLineSegment(sketch, "E438", {"start": v(337.62, 23.78) * mm, "end": v(343.12, 26.8) * mm});
            skLineSegment(sketch, "E439", {"start": v(343.12, 26.8) * mm, "end": v(348.59, 30.13) * mm});
            skLineSegment(sketch, "E440", {"start": v(348.59, 30.13) * mm, "end": v(354, 33.72) * mm});
            skLineSegment(sketch, "E441", {"start": v(354, 33.72) * mm, "end": v(351.78, 51.97) * mm});
            skLineSegment(sketch, "E442", {"start": v(351.78, 51.97) * mm, "end": v(345.67, 54.17) * mm});
            skLineSegment(sketch, "E443", {"start": v(345.67, 54.17) * mm, "end": v(339.57, 56.08) * mm});
            skLineSegment(sketch, "E444", {"start": v(339.57, 56.08) * mm, "end": v(333.5, 57.71) * mm});
            skLineSegment(sketch, "E445", {"start": v(333.5, 57.71) * mm, "end": v(327.46, 59.04) * mm});
            skLineSegment(sketch, "E446", {"start": v(327.46, 59.04) * mm, "end": v(321.47, 60.03) * mm});
            skLineSegment(sketch, "E447", {"start": v(321.47, 60.03) * mm, "end": v(315.53, 60.66) * mm});
            skLineSegment(sketch, "E448", {"start": v(315.53, 60.66) * mm, "end": v(309.67, 60.86) * mm});
            skLineSegment(sketch, "E449", {"start": v(309.67, 60.86) * mm, "end": v(303.93, 60.45) * mm});
            skLineSegment(sketch, "E450", {"start": v(303.93, 60.45) * mm, "end": v(298.11, 60.38) * mm});
            skLineSegment(sketch, "E451", {"start": v(298.11, 60.38) * mm, "end": v(289.78, 71.42) * mm});
            skLineSegment(sketch, "E452", {"start": v(289.78, 71.42) * mm, "end": v(292.02, 85.08) * mm});
            skLineSegment(sketch, "E453", {"start": v(292.02, 85.08) * mm, "end": v(297.2, 87.72) * mm});
            skLineSegment(sketch, "E454", {"start": v(297.2, 87.72) * mm, "end": v(302.48, 90.02) * mm});
            skLineSegment(sketch, "E455", {"start": v(302.48, 90.02) * mm, "end": v(307.58, 92.92) * mm});
            skLineSegment(sketch, "E456", {"start": v(307.58, 92.92) * mm, "end": v(312.54, 96.24) * mm});
            skLineSegment(sketch, "E457", {"start": v(312.54, 96.24) * mm, "end": v(317.39, 99.9) * mm});
            skLineSegment(sketch, "E458", {"start": v(317.39, 99.9) * mm, "end": v(322.12, 103.88) * mm});
            skLineSegment(sketch, "E459", {"start": v(322.12, 103.88) * mm, "end": v(326.74, 108.15) * mm});
            skLineSegment(sketch, "E460", {"start": v(326.74, 108.15) * mm, "end": v(331.25, 112.68) * mm});
            skLineSegment(sketch, "E461", {"start": v(331.25, 112.68) * mm, "end": v(335.64, 117.46) * mm});
            skLineSegment(sketch, "E462", {"start": v(335.64, 117.46) * mm, "end": v(329.12, 134.65) * mm});
            skLineSegment(sketch, "E463", {"start": v(329.12, 134.65) * mm, "end": v(322.66, 135.32) * mm});
            skLineSegment(sketch, "E464", {"start": v(322.66, 135.32) * mm, "end": v(316.28, 135.72) * mm});
            skLineSegment(sketch, "E465", {"start": v(316.28, 135.72) * mm, "end": v(310, 135.85) * mm});
            skLineSegment(sketch, "E466", {"start": v(310, 135.85) * mm, "end": v(303.82, 135.69) * mm});
            skLineSegment(sketch, "E467", {"start": v(303.82, 135.69) * mm, "end": v(297.76, 135.22) * mm});
            skLineSegment(sketch, "E468", {"start": v(297.76, 135.22) * mm, "end": v(291.85, 134.41) * mm});
            skLineSegment(sketch, "E469", {"start": v(291.85, 134.41) * mm, "end": v(286.1, 133.2) * mm});
            skLineSegment(sketch, "E470", {"start": v(286.1, 133.2) * mm, "end": v(280.63, 131.43) * mm});
            skLineSegment(sketch, "E471", {"start": v(280.63, 131.43) * mm, "end": v(275, 129.97) * mm});
            skLineSegment(sketch, "E472", {"start": v(275, 129.97) * mm, "end": v(264.26, 138.7) * mm});
            skLineSegment(sketch, "E473", {"start": v(264.26, 138.7) * mm, "end": v(263.18, 152.49) * mm});
            skLineSegment(sketch, "E474", {"start": v(263.18, 152.49) * mm, "end": v(267.58, 156.3) * mm});
            skLineSegment(sketch, "E475", {"start": v(267.58, 156.3) * mm, "end": v(272.15, 159.8) * mm});
            skLineSegment(sketch, "E476", {"start": v(272.15, 159.8) * mm, "end": v(276.4, 163.83) * mm});
            skLineSegment(sketch, "E477", {"start": v(276.4, 163.83) * mm, "end": v(280.43, 168.24) * mm});
            skLineSegment(sketch, "E478", {"start": v(280.43, 168.24) * mm, "end": v(284.26, 172.96) * mm});
            skLineSegment(sketch, "E479", {"start": v(284.26, 172.96) * mm, "end": v(287.9, 177.95) * mm});
            skLineSegment(sketch, "E480", {"start": v(287.9, 177.95) * mm, "end": v(291.36, 183.2) * mm});
            skLineSegment(sketch, "E481", {"start": v(291.36, 183.2) * mm, "end": v(294.65, 188.67) * mm});
            skLineSegment(sketch, "E482", {"start": v(294.65, 188.67) * mm, "end": v(297.78, 194.37) * mm});
            skLineSegment(sketch, "E483", {"start": v(297.78, 194.37) * mm, "end": v(287.33, 209.5) * mm});
            skLineSegment(sketch, "E484", {"start": v(287.33, 209.5) * mm, "end": v(280.9, 208.6) * mm});
            skLineSegment(sketch, "E485", {"start": v(280.9, 208.6) * mm, "end": v(274.61, 207.47) * mm});
            skLineSegment(sketch, "E486", {"start": v(274.61, 207.47) * mm, "end": v(268.48, 206.09) * mm});
            skLineSegment(sketch, "E487", {"start": v(268.48, 206.09) * mm, "end": v(262.52, 204.45) * mm});
            skLineSegment(sketch, "E488", {"start": v(262.52, 204.45) * mm, "end": v(256.75, 202.55) * mm});
            skLineSegment(sketch, "E489", {"start": v(256.75, 202.55) * mm, "end": v(251.2, 200.35) * mm});
            skLineSegment(sketch, "E490", {"start": v(251.2, 200.35) * mm, "end": v(245.92, 197.8) * mm});
            skLineSegment(sketch, "E491", {"start": v(245.92, 197.8) * mm, "end": v(241.02, 194.77) * mm});
            skLineSegment(sketch, "E492", {"start": v(241.02, 194.77) * mm, "end": v(235.9, 192) * mm});
            skLineSegment(sketch, "E493", {"start": v(235.9, 192) * mm, "end": v(223.4, 197.9) * mm});
            skLineSegment(sketch, "E494", {"start": v(223.4, 197.9) * mm, "end": v(219.04, 211.04) * mm});
            skLineSegment(sketch, "E495", {"start": v(219.04, 211.04) * mm, "end": v(222.4, 215.79) * mm});
            skLineSegment(sketch, "E496", {"start": v(222.4, 215.79) * mm, "end": v(226, 220.28) * mm});
            skLineSegment(sketch, "E497", {"start": v(226, 220.28) * mm, "end": v(229.17, 225.22) * mm});
            skLineSegment(sketch, "E498", {"start": v(229.17, 225.22) * mm, "end": v(232.02, 230.46) * mm});
            skLineSegment(sketch, "E499", {"start": v(232.02, 230.46) * mm, "end": v(234.6, 235.96) * mm});
            skLineSegment(sketch, "E500", {"start": v(234.6, 235.96) * mm, "end": v(236.94, 241.68) * mm});
            skLineSegment(sketch, "E501", {"start": v(236.94, 241.68) * mm, "end": v(239.05, 247.6) * mm});
            skLineSegment(sketch, "E502", {"start": v(239.05, 247.6) * mm, "end": v(240.94, 253.7) * mm});
            skLineSegment(sketch, "E503", {"start": v(240.94, 253.7) * mm, "end": v(242.6, 259.99) * mm});
            skLineSegment(sketch, "E504", {"start": v(242.6, 259.99) * mm, "end": v(228.85, 272.18) * mm});
            skLineSegment(sketch, "E505", {"start": v(228.85, 272.18) * mm, "end": v(222.82, 269.76) * mm});
            skLineSegment(sketch, "E506", {"start": v(222.82, 269.76) * mm, "end": v(216.98, 267.16) * mm});
            skLineSegment(sketch, "E507", {"start": v(216.98, 267.16) * mm, "end": v(211.36, 264.35) * mm});
            skLineSegment(sketch, "E508", {"start": v(211.36, 264.35) * mm, "end": v(205.96, 261.34) * mm});
            skLineSegment(sketch, "E509", {"start": v(205.96, 261.34) * mm, "end": v(200.81, 258.1) * mm});
            skLineSegment(sketch, "E510", {"start": v(200.81, 258.1) * mm, "end": v(195.95, 254.64) * mm});
            skLineSegment(sketch, "E511", {"start": v(195.95, 254.64) * mm, "end": v(191.43, 250.9) * mm});
            skLineSegment(sketch, "E512", {"start": v(191.43, 250.9) * mm, "end": v(187.4, 246.79) * mm});
            skLineSegment(sketch, "E513", {"start": v(187.4, 246.79) * mm, "end": v(183.1, 242.88) * mm});
            skLineSegment(sketch, "E514", {"start": v(183.1, 242.88) * mm, "end": v(169.54, 245.62) * mm});
            skLineSegment(sketch, "E515", {"start": v(169.54, 245.62) * mm, "end": v(162.17, 257.33) * mm});
            skLineSegment(sketch, "E516", {"start": v(162.17, 257.33) * mm, "end": v(164.3, 262.74) * mm});
            skLineSegment(sketch, "E517", {"start": v(164.3, 262.74) * mm, "end": v(166.72, 267.97) * mm});
            skLineSegment(sketch, "E518", {"start": v(166.72, 267.97) * mm, "end": v(168.6, 273.52) * mm});
            skLineSegment(sketch, "E519", {"start": v(168.6, 273.52) * mm, "end": v(170.12, 279.3) * mm});
            skLineSegment(sketch, "E520", {"start": v(170.12, 279.3) * mm, "end": v(171.32, 285.25) * mm});
            skLineSegment(sketch, "E521", {"start": v(171.32, 285.25) * mm, "end": v(172.22, 291.36) * mm});
            skLineSegment(sketch, "E522", {"start": v(172.22, 291.36) * mm, "end": v(172.85, 297.62) * mm});
            skLineSegment(sketch, "E523", {"start": v(172.85, 297.62) * mm, "end": v(173.22, 304) * mm});
            skLineSegment(sketch, "E524", {"start": v(173.22, 304) * mm, "end": v(173.34, 310.5) * mm});
            skLineSegment(sketch, "E525", {"start": v(173.34, 310.5) * mm, "end": v(157.06, 319.03) * mm});
            skLineSegment(sketch, "E526", {"start": v(157.06, 319.03) * mm, "end": v(151.78, 315.25) * mm});
            skLineSegment(sketch, "E527", {"start": v(151.78, 315.25) * mm, "end": v(146.74, 311.32) * mm});
            skLineSegment(sketch, "E528", {"start": v(146.74, 311.32) * mm, "end": v(141.95, 307.25) * mm});
            skLineSegment(sketch, "E529", {"start": v(141.95, 307.25) * mm, "end": v(137.43, 303.03) * mm});
            skLineSegment(sketch, "E530", {"start": v(137.43, 303.03) * mm, "end": v(133.21, 298.66) * mm});
            skLineSegment(sketch, "E531", {"start": v(133.21, 298.66) * mm, "end": v(129.32, 294.14) * mm});
            skLineSegment(sketch, "E532", {"start": v(129.32, 294.14) * mm, "end": v(125.83, 289.43) * mm});
            skLineSegment(sketch, "E533", {"start": v(125.83, 289.43) * mm, "end": v(122.9, 284.47) * mm});
            skLineSegment(sketch, "E534", {"start": v(122.9, 284.47) * mm, "end": v(119.65, 279.64) * mm});
            skLineSegment(sketch, "E535", {"start": v(119.65, 279.64) * mm, "end": v(105.83, 279.06) * mm});
            skLineSegment(sketch, "E536", {"start": v(105.83, 279.06) * mm, "end": v(95.87, 288.66) * mm});
            skLineSegment(sketch, "E537", {"start": v(95.87, 288.66) * mm, "end": v(96.64, 294.42) * mm});
            skLineSegment(sketch, "E538", {"start": v(96.64, 294.42) * mm, "end": v(97.74, 300.08) * mm});
            skLineSegment(sketch, "E539", {"start": v(97.74, 300.08) * mm, "end": v(98.25, 305.92) * mm});
            skLineSegment(sketch, "E540", {"start": v(98.25, 305.92) * mm, "end": v(98.34, 311.89) * mm});
            skLineSegment(sketch, "E541", {"start": v(98.34, 311.89) * mm, "end": v(98.08, 317.96) * mm});
            skLineSegment(sketch, "E542", {"start": v(98.08, 317.96) * mm, "end": v(97.5, 324.11) * mm});
            skLineSegment(sketch, "E543", {"start": v(97.5, 324.11) * mm, "end": v(96.6, 330.33) * mm});
            skLineSegment(sketch, "E544", {"start": v(96.6, 330.33) * mm, "end": v(95.44, 336.62) * mm});
            skLineSegment(sketch, "E545", {"start": v(95.44, 336.62) * mm, "end": v(94, 342.95) * mm});
            skLineSegment(sketch, "E546", {"start": v(94, 342.95) * mm, "end": v(76.15, 347.35) * mm});
            skLineSegment(sketch, "E547", {"start": v(53.18, 311.88) * mm, "end": v(55.27, 318.4) * mm});
            skLineSegment(sketch, "E548", {"start": v(303.82, 176.2) * mm, "end": v(297.88, 174.2) * mm});
            skLineSegment(sketch, "E549", {"start": v(297.88, 174.2) * mm, "end": v(291.93, 171.69) * mm});
            skLineSegment(sketch, "E550", {"start": v(291.93, 171.69) * mm, "end": v(286, 168.67) * mm});
            skLineSegment(sketch, "E551", {"start": v(286, 168.67) * mm, "end": v(280.1, 165.18) * mm});
            skLineSegment(sketch, "E552", {"start": v(280.1, 165.18) * mm, "end": v(280.1, 148.78) * mm});
            skLineSegment(sketch, "E553", {"start": v(280.1, 148.78) * mm, "end": v(286, 145.29) * mm});
            skLineSegment(sketch, "E554", {"start": v(286, 145.29) * mm, "end": v(291.93, 142.27) * mm});
            skLineSegment(sketch, "E555", {"start": v(291.93, 142.27) * mm, "end": v(297.88, 139.75) * mm});
            skLineSegment(sketch, "E556", {"start": v(297.88, 139.75) * mm, "end": v(303.82, 137.77) * mm});
            skLineSegment(sketch, "E557", {"start": v(303.82, 137.77) * mm, "end": v(309.73, 136.38) * mm});
            skLineSegment(sketch, "E558", {"start": v(309.73, 136.38) * mm, "end": v(315.57, 135.75) * mm});
            skLineSegment(sketch, "E559", {"start": v(315.57, 135.75) * mm, "end": v(321.2, 136.76) * mm});
            skLineSegment(sketch, "E560", {"start": v(321.2, 136.76) * mm, "end": v(326.89, 137.31) * mm});
            skLineSegment(sketch, "E561", {"start": v(326.89, 137.31) * mm, "end": v(332.73, 136.7) * mm});
            skLineSegment(sketch, "E562", {"start": v(332.73, 136.7) * mm, "end": v(340.75, 124.48) * mm});
            skLineSegment(sketch, "E563", {"start": v(340.75, 124.48) * mm, "end": v(338.83, 110) * mm});
            skLineSegment(sketch, "E564", {"start": v(338.83, 110) * mm, "end": v(333.83, 106.9) * mm});
            skLineSegment(sketch, "E565", {"start": v(333.83, 106.9) * mm, "end": v(328.46, 104.94) * mm});
            skLineSegment(sketch, "E566", {"start": v(328.46, 104.94) * mm, "end": v(322.95, 103.4) * mm});
            skLineSegment(sketch, "E567", {"start": v(322.95, 103.4) * mm, "end": v(317.97, 100.3) * mm});
            skLineSegment(sketch, "E568", {"start": v(317.97, 100.3) * mm, "end": v(313.24, 96.49) * mm});
            skLineSegment(sketch, "E569", {"start": v(313.24, 96.49) * mm, "end": v(308.75, 92.12) * mm});
            skLineSegment(sketch, "E570", {"start": v(308.75, 92.12) * mm, "end": v(304.48, 87.27) * mm});
            skLineSegment(sketch, "E571", {"start": v(304.48, 87.27) * mm, "end": v(300.45, 81.98) * mm});
            skLineSegment(sketch, "E572", {"start": v(300.45, 81.98) * mm, "end": v(296.65, 76.28) * mm});
            skLineSegment(sketch, "E573", {"start": v(296.65, 76.28) * mm, "end": v(303.77, 61.5) * mm});
            skLineSegment(sketch, "E574", {"start": v(303.77, 61.5) * mm, "end": v(310.6, 60.91) * mm});
            skLineSegment(sketch, "E575", {"start": v(310.6, 60.91) * mm, "end": v(317.25, 60.77) * mm});
            skLineSegment(sketch, "E576", {"start": v(317.25, 60.77) * mm, "end": v(323.7, 61.08) * mm});
            skLineSegment(sketch, "E577", {"start": v(323.7, 61.08) * mm, "end": v(329.92, 61.87) * mm});
            skLineSegment(sketch, "E578", {"start": v(329.92, 61.87) * mm, "end": v(335.84, 63.18) * mm});
            skLineSegment(sketch, "E579", {"start": v(-181.82, -296.98) * mm, "end": v(-177.52, -293.2) * mm});
            skLineSegment(sketch, "E580", {"start": v(-177.52, -293.2) * mm, "end": v(-174.37, -288.25) * mm});
            skLineSegment(sketch, "E581", {"start": v(-174.37, -288.25) * mm, "end": v(-171.77, -282.77) * mm});
            skLineSegment(sketch, "E582", {"start": v(-171.77, -282.77) * mm, "end": v(-169.62, -276.88) * mm});
            skLineSegment(sketch, "E583", {"start": v(-169.62, -276.88) * mm, "end": v(-167.88, -270.66) * mm});
            skLineSegment(sketch, "E584", {"start": v(-167.88, -270.66) * mm, "end": v(-166.54, -264.14) * mm});
            skLineSegment(sketch, "E585", {"start": v(-166.54, -264.14) * mm, "end": v(-165.6, -257.36) * mm});
            skLineSegment(sketch, "E586", {"start": v(-165.6, -257.36) * mm, "end": v(-178.42, -247.13) * mm});
            skLineSegment(sketch, "E587", {"start": v(-178.42, -247.13) * mm, "end": v(-184.82, -249.56) * mm});
            skLineSegment(sketch, "E588", {"start": v(-184.82, -249.56) * mm, "end": v(-190.88, -252.32) * mm});
            skLineSegment(sketch, "E589", {"start": v(-190.88, -252.32) * mm, "end": v(-196.56, -255.4) * mm});
            skLineSegment(sketch, "E590", {"start": v(-196.56, -255.4) * mm, "end": v(-201.81, -258.8) * mm});
            skLineSegment(sketch, "E591", {"start": v(-201.81, -258.8) * mm, "end": v(-206.58, -262.56) * mm});
            skLineSegment(sketch, "E592", {"start": v(-206.58, -262.56) * mm, "end": v(-210.72, -266.73) * mm});
            skLineSegment(sketch, "E593", {"start": v(-210.72, -266.73) * mm, "end": v(-213.44, -271.76) * mm});
            skLineSegment(sketch, "E594", {"start": v(-296.65, 76.28) * mm, "end": v(-300.45, 81.98) * mm});
            skLineSegment(sketch, "E595", {"start": v(-300.45, 81.98) * mm, "end": v(-304.49, 87.27) * mm});
            skLineSegment(sketch, "E596", {"start": v(-304.49, 87.27) * mm, "end": v(-308.75, 92.12) * mm});
            skLineSegment(sketch, "E597", {"start": v(-308.75, 92.12) * mm, "end": v(-313.24, 96.49) * mm});
            skLineSegment(sketch, "E598", {"start": v(-313.24, 96.49) * mm, "end": v(-317.97, 100.3) * mm});
            skLineSegment(sketch, "E599", {"start": v(-317.97, 100.3) * mm, "end": v(-322.95, 103.4) * mm});
            skLineSegment(sketch, "E600", {"start": v(-322.95, 103.4) * mm, "end": v(-328.46, 104.94) * mm});
            skLineSegment(sketch, "E601", {"start": v(-328.46, 104.94) * mm, "end": v(-333.83, 106.9) * mm});
            skLineSegment(sketch, "E602", {"start": v(-333.83, 106.9) * mm, "end": v(-338.83, 110) * mm});
            skSolve(sketch);
        }
        {
            var Q0;
            Q0=makeQuery(id+"F0.imprint","IMPRINT",FACE,{"disambiguationData":[TD([[makeQuery(id+"F0.imprint","IMPRINT",EDGE,{"derivedFrom":sQuery(id+"F0.wireOp",EDGE,"E0")}),1.0]])]});
            extrude(context, id + "F1", {"entities" : qUnion([Q0]), "depth" : 25.4 * mm, "offsetDistance" : 25.4 * mm});
        }
    });
